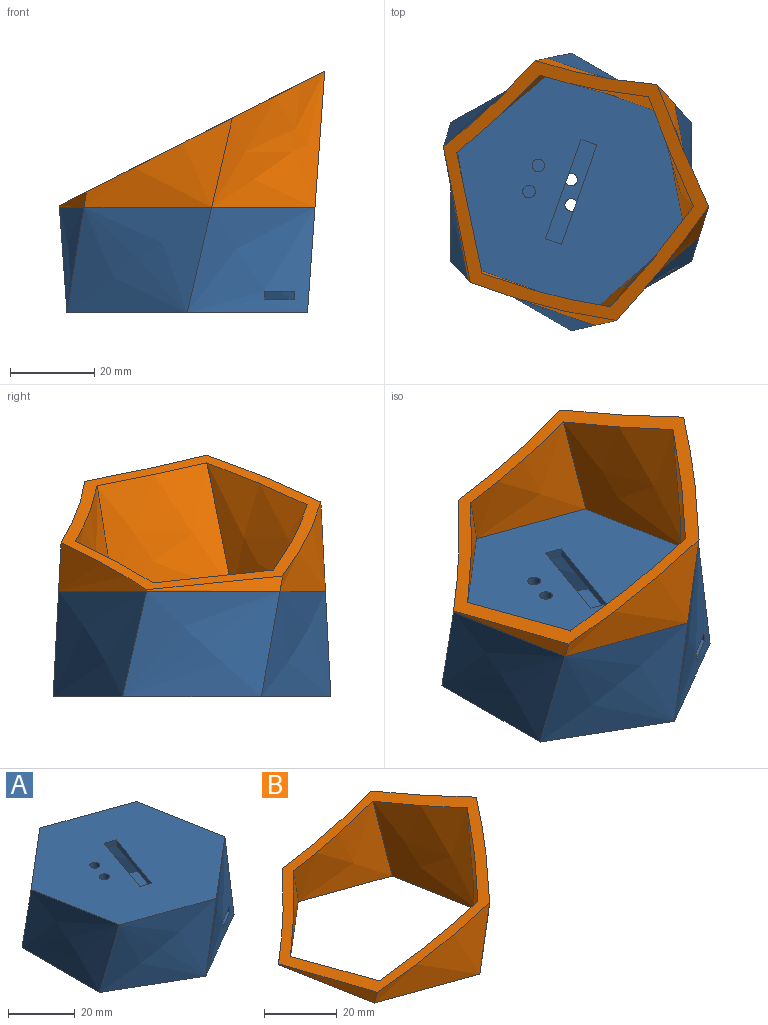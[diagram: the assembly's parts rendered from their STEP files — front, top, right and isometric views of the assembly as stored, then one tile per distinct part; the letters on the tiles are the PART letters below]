
ASSEMBLY  parts=2 mates=1
PART A: 30 faces, bbox 69.6x69.8x64 mm
  f0: offset ~64x36.78mm, area 614.7mm2, adj f2,f3,f4,f5,f23,f24,f25,f26
  f1: plane 0.37x0.11mm, normal (1,0,0), area 0mm2, adj f18,f24,f27
  f2: plane 58.87x55.94mm, normal (0,0,-1), area 2201.9mm2, adj f0,f4,f5,f6,f7,f8,f9,f10
  f3: plane 60.97x53.25mm, normal (0,0,1), area 2401.7mm2, adj f0,f4,f5,f6,f7,f8,f28,f29
  f4: offset ~64x47.41mm, area 633.8mm2, adj f0,f2,f3,f8
  f5: offset ~64x46.41mm, area 633.8mm2, adj f0,f2,f3,f6
  f6: offset ~64x47.41mm, area 633.8mm2, adj f2,f3,f5,f7
  f7: offset ~64x36.78mm, area 633.8mm2, adj f2,f3,f6,f8
  f8: offset ~64x46.41mm, area 633.8mm2, adj f2,f3,f4,f7
  f9: cylinder r=1.5mm len=3mm, axis (0,0,1), area 18.8mm2, adj f2,f15
  f10: cylinder r=1.5mm len=3mm, axis (0,0,1), area 18.8mm2, adj f2,f15
  f11: plane 23.55x8.39mm, normal (0.94,-0.34,0), area 50mm2, adj f2,f12,f14,f15
  f12: plane 3.77x2mm, normal (0.34,0.94,0), area 8mm2, adj f2,f11,f13,f15
  f13: plane 23.55x8.39mm, normal (-0.94,0.34,0), area 50mm2, adj f2,f12,f14,f15
  f14: plane 3.77x2mm, normal (-0.34,-0.94,0), area 8mm2, adj f2,f11,f13,f15
  f15: plane 63.25x60.57mm, normal (0,0,1), area 2571.4mm2, adj f9,f10,f11,f12,f13,f14,f17,f18
  f16: plane 65.82x57mm, normal (0,0,-1), area 2799.6mm2, adj f17,f18,f19,f20,f21,f22,f28,f29
  f17: bspline ~60x43.41mm, area 813.2mm2, adj f15,f16,f18,f22
  f18: bspline ~60x32.78mm, area 796.7mm2, adj f1,f15,f16,f17,f19,f23,f24,f25
  f19: bspline ~60x42.41mm, area 813.2mm2, adj f15,f16,f18,f20
  f20: bspline ~60x43.41mm, area 813.2mm2, adj f15,f16,f19,f21
  f21: bspline ~60x32.78mm, area 813.2mm2, adj f15,f16,f20,f22
  f22: bspline ~60x42.41mm, area 813.2mm2, adj f15,f16,f17,f21
  f23: plane 8.06x6.78mm, normal (0,0,-1), area 17.9mm2, adj f0,f18,f25,f26
  f24: plane 8.04x6.62mm, normal (0,0,1), area 17.6mm2, adj f0,f1,f18,f25,f27
  f25: plane 2.68x2mm, normal (-1,0,0), area 4.7mm2, adj f0,f18,f23,f24
  f26: plane 1.83x1.77mm, normal (0.85,0.53,-0.04), area 3.4mm2, adj f0,f18,f23,f27
  f27: plane 1.69x1.06mm, normal (0.84,0.53,0.12), area 0.6mm2, adj f0,f1,f24,f26
  f28: cylinder r=1.5mm len=3mm, axis (0,0,-1), area 18.8mm2, adj f3,f16
  f29: cylinder r=1.5mm len=3mm, axis (0,0,-1), area 18.8mm2, adj f3,f16
PART B: 14 faces, bbox 71.6x71.8x66 mm
  f0: offset ~66x49.41mm, area 797.3mm2, adj f1,f5,f6,f7
  f1: offset ~66x38.78mm, area 737.9mm2, adj f0,f2,f6,f7
  f2: offset ~66x48.41mm, area 364.6mm2, adj f1,f3,f6,f7
  f3: offset ~66x49.41mm, area 99.6mm2, adj f2,f4,f6,f7
  f4: offset ~66x38.78mm, area 202.6mm2, adj f3,f5,f6,f7
  f5: offset ~66x48.41mm, area 529.1mm2, adj f0,f4,f6,f7
  f6: plane 62.9x61.57mm, normal (-0.45,0,0.89), area 622mm2, adj f0,f1,f2,f3,f4,f5,f8,f9
  f7: plane 63.25x60.57mm, normal (0,0,-1), area 548.5mm2, adj f0,f1,f2,f3,f4,f5,f8,f9
  f8: bspline ~60x43.41mm, area 939.7mm2, adj f6,f7,f9,f13
  f9: bspline ~60x32.78mm, area 869.2mm2, adj f6,f7,f8,f10
  f10: bspline ~60x42.41mm, area 396.1mm2, adj f6,f7,f9,f11
  f11: bspline ~60x43.41mm, area 62.9mm2, adj f6,f7,f10,f12
  f12: bspline ~60x32.78mm, area 195.5mm2, adj f6,f7,f11,f13
  f13: bspline ~60x42.41mm, area 602.8mm2, adj f6,f7,f8,f12
PLACE A t=(19.74,6.32,-20.13)mm
PLACE B t=(19.74,6.32,-20.13)mm
MATE fastened B.f7 <-> A.f15  axis (0,0,-1) through (-10.54,17.11,4.87)mm
